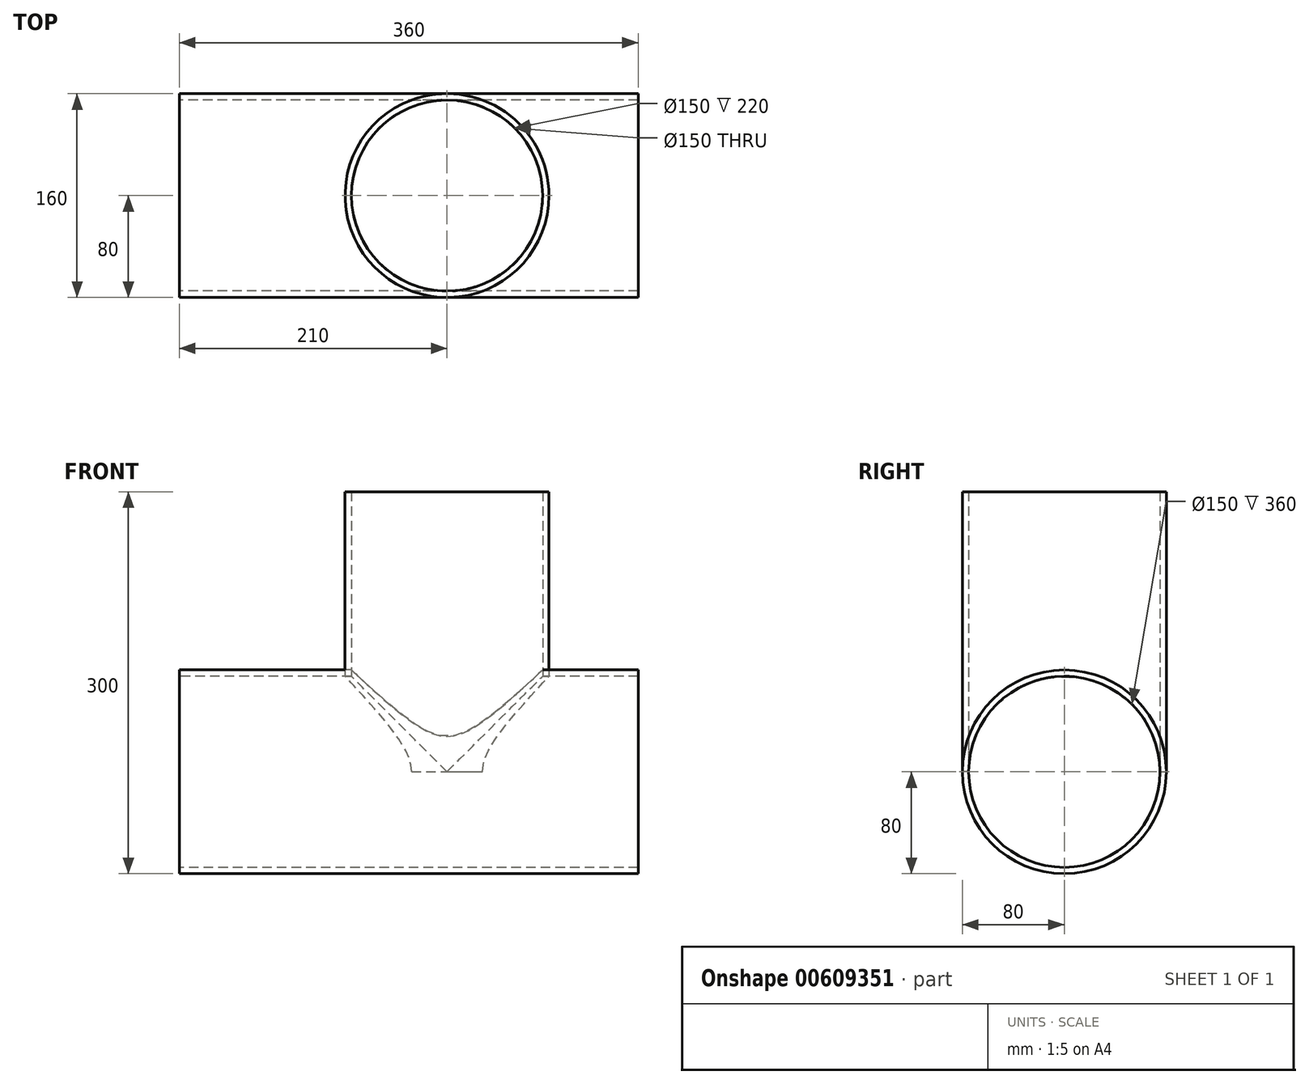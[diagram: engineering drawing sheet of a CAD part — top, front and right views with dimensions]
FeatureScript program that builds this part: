
annotation { "Feature Type Name" : "Feature", "Feature Type Description" : "" }
export const myFeature = defineFeature(function(context is Context, id is Id, definition is map)
    precondition{}
    {
        {
            var Q0;
            Q0=qCreatedBy(makeId("Right.planeOp"),FACE);
            var sketch = newSketch(context, id + "F0", { "sketchPlane" : qUnion([Q0])});
            skCircle(sketch, "E0", {"center": v(0, 0) * mm, "radius": 80 * mm});
            skCircle(sketch, "E1", {"center": v(0, 0) * mm, "radius": 75 * mm});
            skSolve(sketch);
        }
        {
            var Q0;
            Q0=qSketchRegion(id+"F0",true);
            var Q1;
            Q1=makeQuery(id+"F0.imprint","IMPRINT",FACE,{"disambiguationData":[TD([[makeQuery(id+"F0.imprint","IMPRINT",EDGE,{"derivedFrom":sQuery(id+"F0.wireOp",EDGE,"E0")}),1.0]])]});
            extrude(context, id + "F1", {"entities" : qUnion([Q0, Q1]), "endBound" : BoundingType.SYMMETRIC, "depth" : 360 * mm, "offsetDistance" : 25 * mm});
        }
        {
            var Q0;
            Q0=qCreatedBy(makeId("Top.planeOp"),FACE);
            var sketch = newSketch(context, id + "F2", { "sketchPlane" : qUnion([Q0])});
            skCircle(sketch, "E2", {"center": v(0, 0) * mm, "radius": 80 * mm});
            skCircle(sketch, "E3", {"center": v(0, 0) * mm, "radius": 75 * mm});
            skSolve(sketch);
        }
        {
            var Q0;
            Q0=makeQuery(id+"F2.imprint","IMPRINT",FACE,{"disambiguationData":[TD([[makeQuery(id+"F2.imprint","IMPRINT",EDGE,{"derivedFrom":sQuery(id+"F2.wireOp",EDGE,"E2")}),1.0]])]});
            extrude(context, id + "F3", {"entities" : qUnion([Q0]), "depth" : 220 * mm, "offsetDistance" : 25 * mm});
        }
        {
            var Q0;
            Q0=makeQuery(id+"F1.opExtrude","CAP_FACE",FACE,{"disambiguationData":[OSD([sQuery(id+"F0.wireOp",EDGE,"E0"),sQuery(id+"F0.wireOp",EDGE,"E1")])],"isStart":true});
            extrude(context, id + "F4", {"entities" : qUnion([Q0]), "operationType" : NewBodyOperationType.ADD, "depth" : 30 * mm, "offsetDistance" : 25 * mm});
        }
        {
            var Q0;
            Q0=makeQuery(id+"F1.opExtrude","CAP_FACE",FACE,{"disambiguationData":[OSD([sQuery(id+"F0.wireOp",EDGE,"E0"),sQuery(id+"F0.wireOp",EDGE,"E1")])],"isStart":false});
            extrude(context, id + "F5", {"entities" : qUnion([Q0]), "operationType" : NewBodyOperationType.REMOVE, "oppositeDirection" : true, "depth" : 30 * mm, "offsetDistance" : 25 * mm});
        }
        {
            var Q0;
            Q0=qCreatedBy(makeId("Right.planeOp"),FACE);
            var sketch = newSketch(context, id + "F6", { "sketchPlane" : qUnion([Q0])});
            skCircle(sketch, "E4", {"center": v(0, 0) * mm, "radius": 75 * mm});
            skSolve(sketch);
        }
        {
            var Q0;
            Q0 = qSketchRegion(id + "F6", true);
            extrude(context, id + "F7", {"entities" : qUnion([Q0]), "operationType" : NewBodyOperationType.REMOVE, "endBound" : BoundingType.SYMMETRIC, "oppositeDirection" : true, "depth" : 500 * mm, "offsetDistance" : 25 * mm});
        }
        {
            var Q0;
            Q0=qCreatedBy(makeId("Right.planeOp"),FACE);
            var sketch = newSketch(context, id + "F8", { "sketchPlane" : qUnion([Q0])});
            skCircle(sketch, "E5", {"center": v(0, 0) * mm, "radius": 75 * mm});
            skSolve(sketch);
        }
        {
            var Q0;
            Q0=makeQuery(id+"F8.imprint","IMPRINT",FACE,{"disambiguationData":[TD([[makeQuery(id+"F8.imprint","IMPRINT",EDGE,{"derivedFrom":sQuery(id+"F8.wireOp",EDGE,"E5")}),1.0]])]});
            extrude(context, id + "F9", {"entities" : qUnion([Q0]), "operationType" : NewBodyOperationType.REMOVE, "endBound" : BoundingType.SYMMETRIC, "depth" : 500 * mm, "offsetDistance" : 25 * mm});
        }
        {
            var Q0;
            Q0=qCreatedBy(makeId("Top.planeOp"),FACE);
            var sketch = newSketch(context, id + "F10", { "sketchPlane" : qUnion([Q0])});
            skCircle(sketch, "E6", {"center": v(0, 0) * mm, "radius": 75 * mm});
            skSolve(sketch);
        }
        {
            var Q0;
            Q0 = qSketchRegion(id + "F10", true);
            extrude(context, id + "F11", {"entities" : qUnion([Q0]), "operationType" : NewBodyOperationType.REMOVE, "depth" : 500 * mm, "offsetDistance" : 25 * mm});
        }
        {
            var Q0;
            Q0=makeQuery(id+"F1.opExtrude","SWEPT_BODY",BODY,{"disambiguationData":[OSD([sQuery(id+"F0.wireOp",EDGE,"E0"),sQuery(id+"F0.wireOp",EDGE,"E1")])]});
            transform(context, id + "F12", {"entities" : qUnion([Q0]), "transformType" : TransformType.TRANSLATION_3D, "dx" : 0 * mm, "dy" : 0 * mm, "dz" : 0 * mm, "makeCopy" : true});
        }
        {
            var Q0;
            Q0=makeQuery(id+"F12.opPattern","COPY",BODY,{"derivedFrom":makeQuery(id+"F1.opExtrude","SWEPT_BODY",BODY,{"disambiguationData":[OSD([sQuery(id+"F0.wireOp",EDGE,"E0"),sQuery(id+"F0.wireOp",EDGE,"E1")])]}),"instanceName":"1"});
            deleteBodies(context, id + "F13", {"entities" : qUnion([Q0])});
        }
    });
